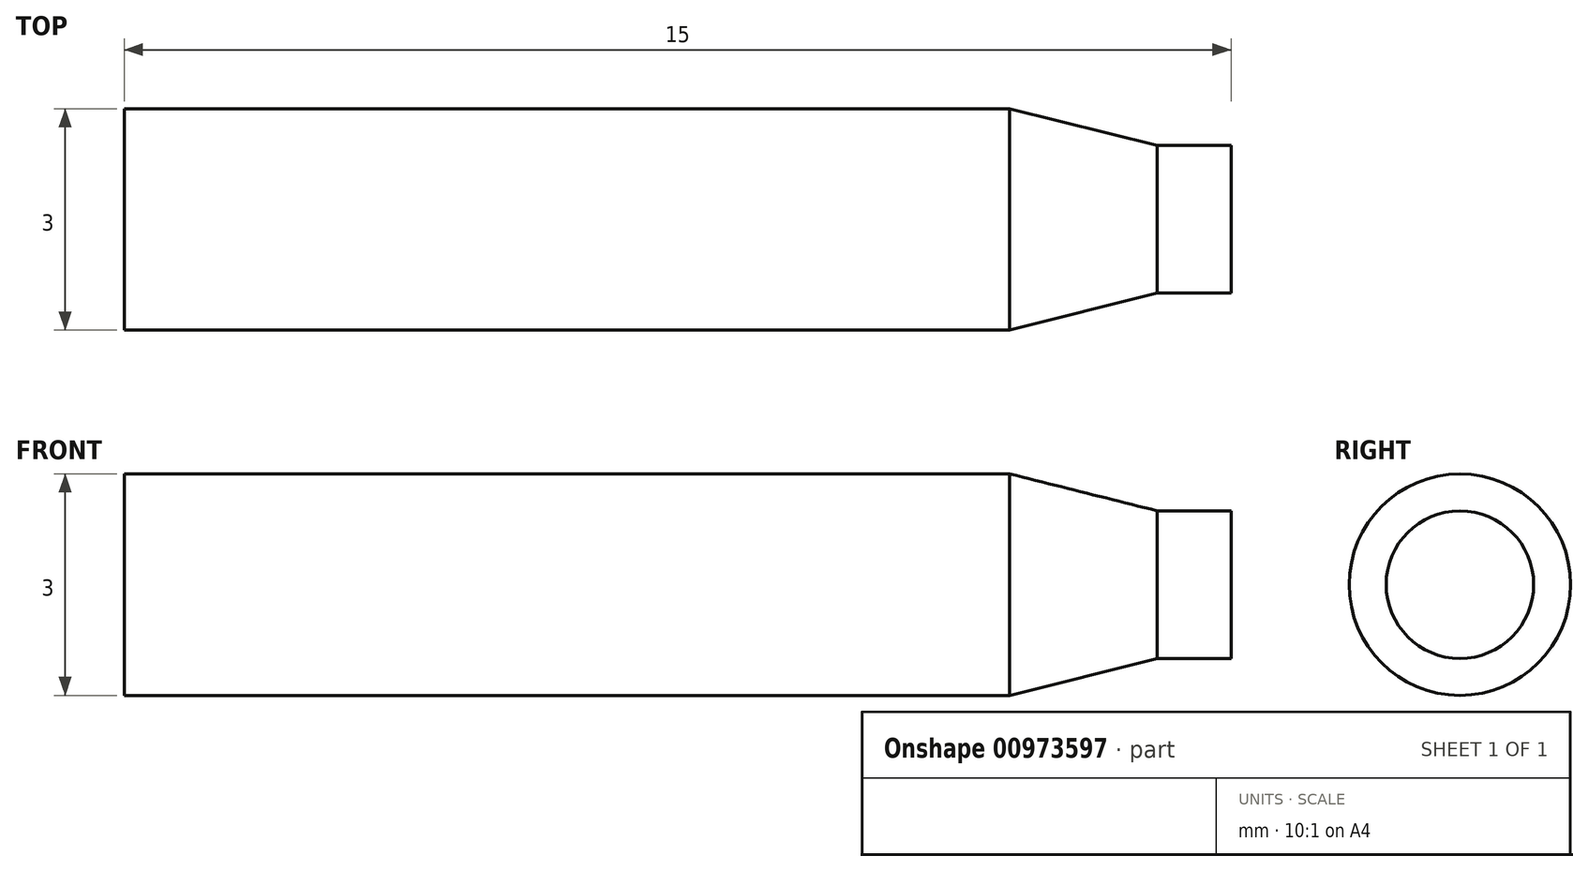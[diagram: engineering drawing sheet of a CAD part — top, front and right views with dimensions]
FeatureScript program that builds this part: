
annotation { "Feature Type Name" : "Feature", "Feature Type Description" : "" }
export const myFeature = defineFeature(function(context is Context, id is Id, definition is map)
    precondition{}
    {
        {
            var Q0;
            Q0=qCreatedBy(makeId("Top.planeOp"),FACE);
            var sketch = newSketch(context, id + "F0", { "sketchPlane" : qUnion([Q0])});
            skLineSegment(sketch, "E0", {"start": v(0, 0) * mm, "end": v(15, 0) * mm});
            skLineSegment(sketch, "E1", {"start": v(15, 0) * mm, "end": v(15, 1) * mm});
            skLineSegment(sketch, "E2", {"start": v(0, 0) * mm, "end": v(0, 1.5) * mm});
            skLineSegment(sketch, "E3", {"start": v(0, 1.5) * mm, "end": v(12, 1.5) * mm});
            skLineSegment(sketch, "E4", {"start": v(12, 1.5) * mm, "end": v(14, 1) * mm});
            skLineSegment(sketch, "E5", {"start": v(14, 1) * mm, "end": v(15, 1) * mm});
            skLineSegment(sketch, "E6", {"start": v(-1.6, 0) * mm, "end": v(16.6, 0) * mm, "construction": true});
            skSolve(sketch);
        }
        {
            var Q0;
            Q0=makeQuery(id+"F0.imprint","IMPRINT",FACE,{"disambiguationData":[TD([[makeQuery(id+"F0.imprint","IMPRINT",EDGE,{"derivedFrom":sQuery(id+"F0.wireOp",EDGE,"E0")}),1.0]])]});
            var Q1;
            Q1=sQuery(id+"F0.wireOp",EDGE,"E0");
            revolve(context, id + "F1", {"surfaceOperationType" : NewSurfaceOperationType.NEW, "entities" : qUnion([Q0]), "axis" : qUnion([Q1]), "revolveType" : RevolveType.FULL});
        }
    });
